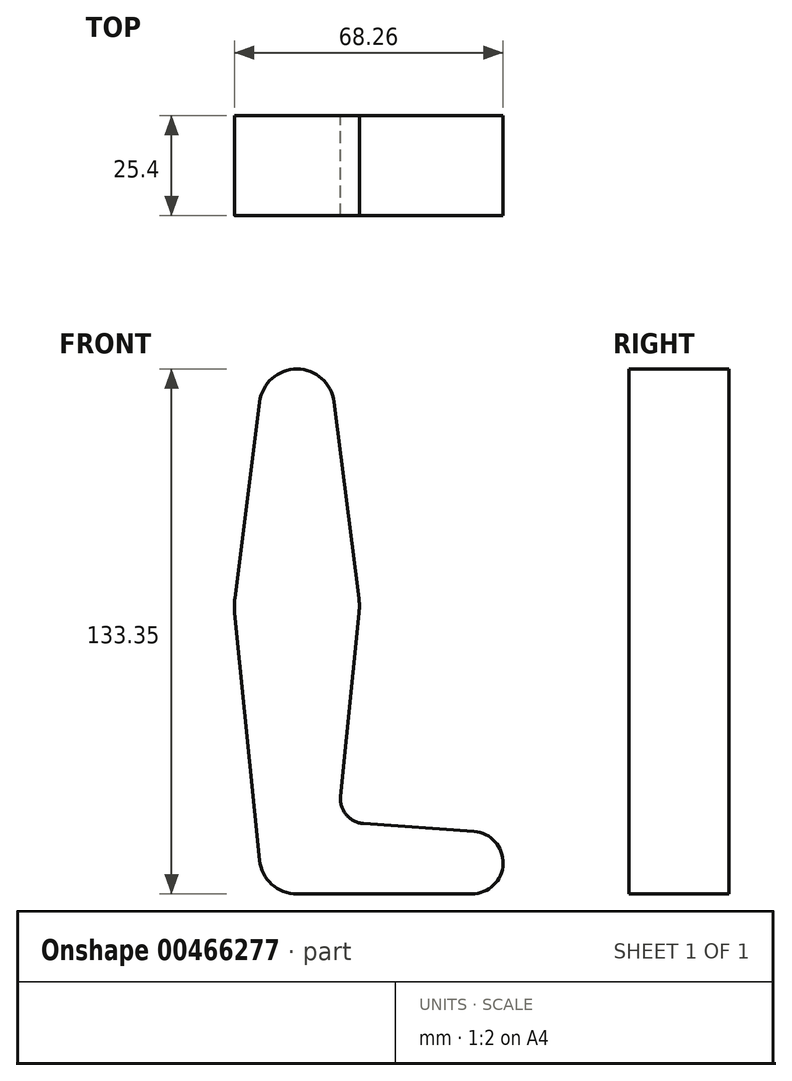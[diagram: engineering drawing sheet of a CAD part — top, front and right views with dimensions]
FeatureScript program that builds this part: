
annotation { "Feature Type Name" : "Feature", "Feature Type Description" : "" }
export const myFeature = defineFeature(function(context is Context, id is Id, definition is map)
    precondition{}
    {
        {
            var Q0;
            Q0=qCreatedBy(makeId("Front.planeOp"),FACE);
            var sketch = newSketch(context, id + "F0", { "sketchPlane" : qUnion([Q0])});
            skCircle(sketch, "E0", {"center": v(0, 92.04) * mm, "radius": 9.53 * mm});
            skCircle(sketch, "E1", {"center": v(0, -22.26) * mm, "radius": 9.53 * mm});
            skCircle(sketch, "E2", {"center": v(0, 41.24) * mm, "radius": 15.88 * mm});
            skCircle(sketch, "E3", {"center": v(44.45, -23.85) * mm, "radius": 7.94 * mm});
            skLineSegment(sketch, "E4", {"start": v(0, -22.26) * mm, "end": v(44.45, -23.85) * mm, "construction": true});
            skLineSegment(sketch, "E5", {"start": v(0, 92.04) * mm, "end": v(0, 41.24) * mm, "construction": true});
            skLineSegment(sketch, "E6", {"start": v(0, 41.24) * mm, "end": v(0, -22.26) * mm, "construction": true});
            skLineSegment(sketch, "E7", {"start": v(-9.45, 93.23) * mm, "end": v(-15.75, 43.22) * mm});
            skLineSegment(sketch, "E8", {"start": v(-15.8, 39.65) * mm, "end": v(-9.48, -23.21) * mm});
            skLineSegment(sketch, "E9", {"start": v(9.45, 93.23) * mm, "end": v(15.75, 43.22) * mm});
            skLineSegment(sketch, "E10", {"start": v(15.8, 39.65) * mm, "end": v(11.11, -6.96) * mm});
            skLineSegment(sketch, "E11", {"start": v(16.98, -13.92) * mm, "end": v(45.02, -15.93) * mm});
            skLineSegment(sketch, "E12", {"start": v(0, -31.79) * mm, "end": v(45.02, -31.79) * mm});
            skPoint(sketch, "E13.newPointB", {"position": v(0, -12.71) * mm});
            skArc(sketch, "E13.filletArc", {"start": v(11.11, -6.96) * mm, "mid": v(12.57, -11.68) * mm, "end": v(16.98, -13.92) * mm});
            skSolve(sketch);
        }
        {
            var Q0;
            Q0 = qSketchRegion(id + "F0", true);
            extrude(context, id + "F1", {"entities" : qUnion([Q0]), "depth" : 25.4 * mm, "offsetDistance" : 25.4 * mm});
        }
    });
